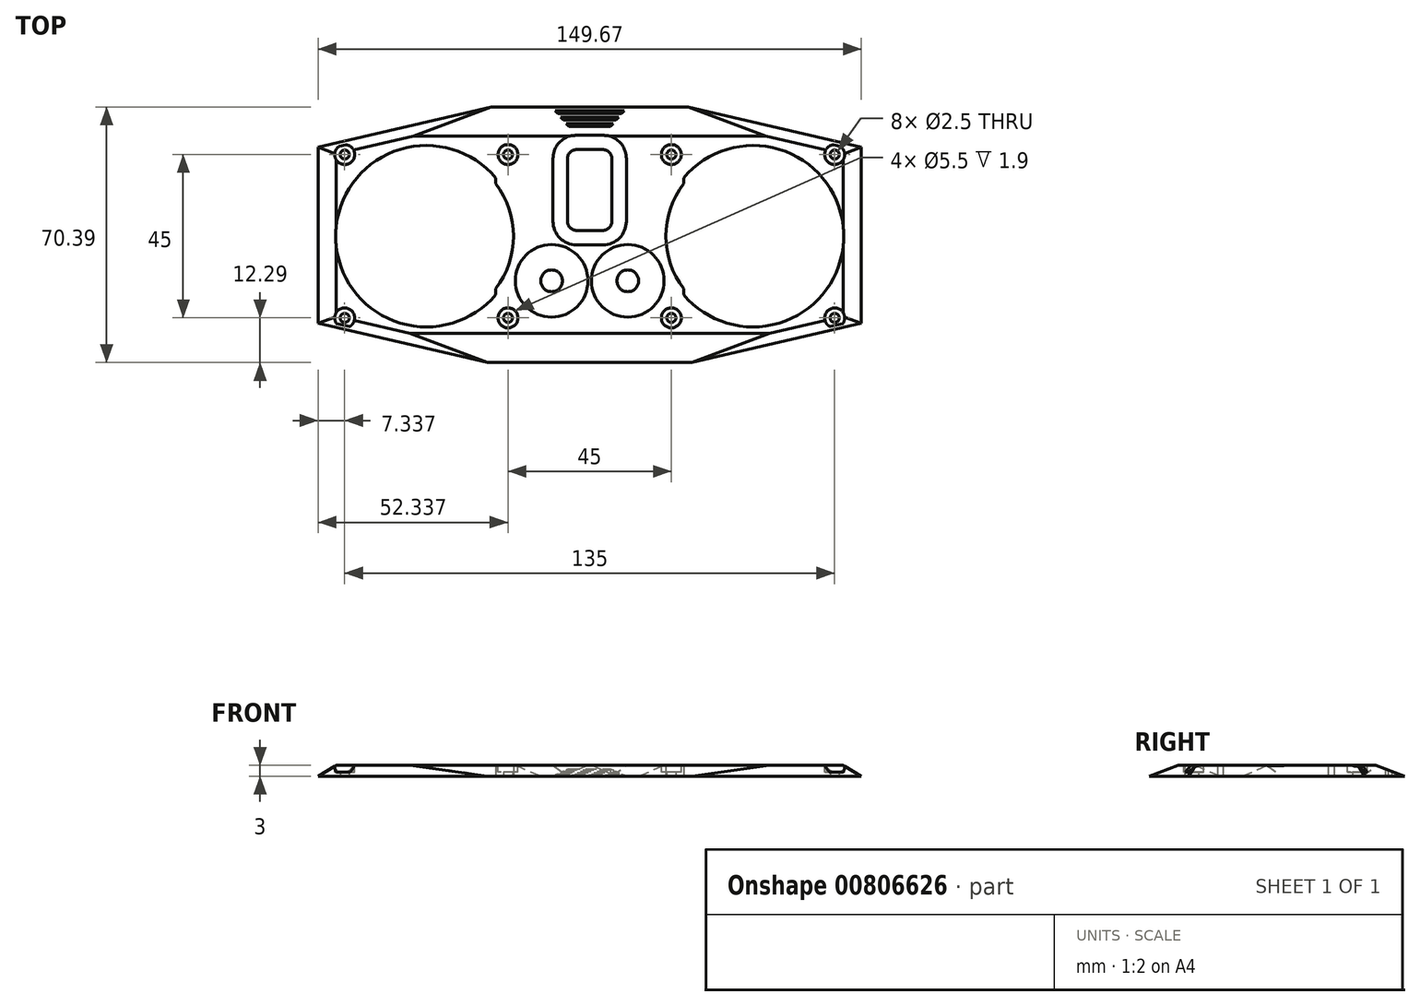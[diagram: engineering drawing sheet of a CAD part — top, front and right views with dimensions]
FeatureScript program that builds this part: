
annotation { "Feature Type Name" : "Feature", "Feature Type Description" : "" }
export const myFeature = defineFeature(function(context is Context, id is Id, definition is map)
    precondition{}
    {
        {
            var Q0;
            Q0=qCreatedBy(makeId("Top.planeOp"),FACE);
            var sketch = newSketch(context, id + "F0", { "sketchPlane" : qUnion([Q0])});
            skArc(sketch, "E0.0", {"start": v(-27.05, 29.93) * mm, "mid": v(-71.2, 13.86) * mm, "end": v(-27.05, -2.2) * mm});
            skArc(sketch, "E0.1", {"start": v(-27.05, -0.6) * mm, "mid": v(-22.2, 13.86) * mm, "end": v(-27.05, 28.32) * mm});
            skLineSegment(sketch, "E0.2", {"start": v(-27.05, -2.2) * mm, "end": v(-27.05, -0.6) * mm});
            skLineSegment(sketch, "E0.3", {"start": v(-27.05, 29.93) * mm, "end": v(-27.05, 28.32) * mm});
            skCircle(sketch, "E0.4", {"center": v(-23.7, 36.36) * mm, "radius": 1.25 * mm});
            skCircle(sketch, "E0.5", {"center": v(-68.7, 36.36) * mm, "radius": 1.25 * mm});
            skLineSegment(sketch, "E0.6", {"start": v(-77.2, 39.39) * mm, "end": v(-28.53, 50.62) * mm, "construction": true});
            skLineSegment(sketch, "E0.7", {"start": v(-77.2, 39.39) * mm, "end": v(-77.2, -45.78) * mm, "construction": true});
            skLineSegment(sketch, "E0.8", {"start": v(-28.53, 50.62) * mm, "end": v(26.12, 50.62) * mm, "construction": true});
            skLineSegment(sketch, "E0.9", {"start": v(74.8, 39.39) * mm, "end": v(26.12, 50.62) * mm, "construction": true});
            skLineSegment(sketch, "E0.10", {"start": v(-12.2, 50.26) * mm, "end": v(9.8, 50.26) * mm, "construction": true});
            skLineSegment(sketch, "E0.11", {"start": v(-11.4, 49.46) * mm, "end": v(9, 49.46) * mm, "construction": true});
            skLineSegment(sketch, "E0.12", {"start": v(8.3, 48.46) * mm, "end": v(-10.7, 48.46) * mm});
            skLineSegment(sketch, "E0.13", {"start": v(7.5, 47.66) * mm, "end": v(-9.9, 47.66) * mm});
            skLineSegment(sketch, "E0.14", {"start": v(6.8, 46.66) * mm, "end": v(-9.2, 46.66) * mm});
            skLineSegment(sketch, "E0.15", {"start": v(6, 45.86) * mm, "end": v(-8.4, 45.86) * mm});
            skLineSegment(sketch, "E0.16", {"start": v(5.3, 44.86) * mm, "end": v(-7.7, 44.86) * mm});
            skLineSegment(sketch, "E0.17", {"start": v(4.5, 44.06) * mm, "end": v(-6.9, 44.06) * mm});
            skLineSegment(sketch, "E0.18", {"start": v(-5.3, 35.25) * mm, "end": v(-5.3, 17.95) * mm, "construction": true});
            skLineSegment(sketch, "E0.19", {"start": v(2.4, 35.75) * mm, "end": v(-4.8, 35.75) * mm, "construction": true});
            skLineSegment(sketch, "E0.20", {"start": v(2.9, 35.25) * mm, "end": v(2.9, 17.95) * mm, "construction": true});
            skLineSegment(sketch, "E0.21", {"start": v(2.4, 17.45) * mm, "end": v(-4.8, 17.45) * mm, "construction": true});
            skArc(sketch, "E0.22", {"start": v(-4.8, 17.45) * mm, "mid": v(-5.16, 17.6) * mm, "end": v(-5.3, 17.95) * mm, "construction": true});
            skArc(sketch, "E0.23", {"start": v(2.9, 17.95) * mm, "mid": v(2.75, 17.6) * mm, "end": v(2.4, 17.45) * mm, "construction": true});
            skArc(sketch, "E0.24", {"start": v(2.4, 35.75) * mm, "mid": v(2.75, 35.6) * mm, "end": v(2.9, 35.25) * mm, "construction": true});
            skArc(sketch, "E0.25", {"start": v(-5.3, 35.25) * mm, "mid": v(-5.16, 35.6) * mm, "end": v(-4.8, 35.75) * mm, "construction": true});
            skCircle(sketch, "E0.26", {"center": v(21.3, 36.36) * mm, "radius": 1.25 * mm});
            skCircle(sketch, "E0.27", {"center": v(66.3, 36.36) * mm, "radius": 1.25 * mm});
            skCircle(sketch, "E0.28", {"center": v(66.3, -8.64) * mm, "radius": 1.25 * mm});
            skCircle(sketch, "E0.29", {"center": v(21.3, -8.64) * mm, "radius": 1.25 * mm});
            skArc(sketch, "E0.30", {"start": v(24.64, -2.2) * mm, "mid": v(68.8, 13.86) * mm, "end": v(24.64, 29.93) * mm});
            skArc(sketch, "E0.31", {"start": v(24.64, 28.32) * mm, "mid": v(19.8, 13.86) * mm, "end": v(24.64, -0.6) * mm});
            skLineSegment(sketch, "E0.32", {"start": v(74.8, -45.78) * mm, "end": v(74.8, 39.39) * mm, "construction": true});
            skLineSegment(sketch, "E0.33", {"start": v(24.64, -2.2) * mm, "end": v(24.64, -0.6) * mm});
            skLineSegment(sketch, "E0.34", {"start": v(24.64, 29.93) * mm, "end": v(24.64, 28.32) * mm});
            skLineSegment(sketch, "E0.35", {"start": v(13.5, 10.27) * mm, "end": v(5.1, 10.27) * mm, "construction": true});
            skLineSegment(sketch, "E0.36", {"start": v(13.5, 5.77) * mm, "end": v(13.5, 10.27) * mm, "construction": true});
            skLineSegment(sketch, "E0.37", {"start": v(18, 5.77) * mm, "end": v(13.5, 5.77) * mm, "construction": true});
            skLineSegment(sketch, "E0.38", {"start": v(18, -2.63) * mm, "end": v(18, 5.77) * mm, "construction": true});
            skLineSegment(sketch, "E0.39", {"start": v(13.5, -2.63) * mm, "end": v(18, -2.63) * mm, "construction": true});
            skLineSegment(sketch, "E0.40", {"start": v(13.5, -7.13) * mm, "end": v(13.5, -2.63) * mm, "construction": true});
            skLineSegment(sketch, "E0.41", {"start": v(13.5, -7.13) * mm, "end": v(5.1, -7.13) * mm, "construction": true});
            skLineSegment(sketch, "E0.42", {"start": v(5.1, -7.13) * mm, "end": v(5.1, -2.63) * mm, "construction": true});
            skLineSegment(sketch, "E0.43", {"start": v(0.6, -2.63) * mm, "end": v(5.1, -2.63) * mm, "construction": true});
            skLineSegment(sketch, "E0.44", {"start": v(0.6, -2.63) * mm, "end": v(0.6, 5.77) * mm, "construction": true});
            skLineSegment(sketch, "E0.45", {"start": v(5.1, 5.77) * mm, "end": v(0.6, 5.77) * mm, "construction": true});
            skLineSegment(sketch, "E0.46", {"start": v(5.1, 5.77) * mm, "end": v(5.1, 10.27) * mm, "construction": true});
            skLineSegment(sketch, "E0.47", {"start": v(-3, -2.63) * mm, "end": v(-3, 5.77) * mm, "construction": true});
            skLineSegment(sketch, "E0.48", {"start": v(-7.5, 5.77) * mm, "end": v(-3, 5.77) * mm, "construction": true});
            skLineSegment(sketch, "E0.49", {"start": v(-7.5, 5.77) * mm, "end": v(-7.5, 10.27) * mm, "construction": true});
            skLineSegment(sketch, "E0.50", {"start": v(-15.9, 10.27) * mm, "end": v(-7.5, 10.27) * mm, "construction": true});
            skLineSegment(sketch, "E0.51", {"start": v(-15.9, 5.77) * mm, "end": v(-15.9, 10.27) * mm, "construction": true});
            skLineSegment(sketch, "E0.52", {"start": v(-20.4, 5.77) * mm, "end": v(-15.9, 5.77) * mm, "construction": true});
            skLineSegment(sketch, "E0.53", {"start": v(-20.4, -2.63) * mm, "end": v(-20.4, 5.77) * mm, "construction": true});
            skLineSegment(sketch, "E0.54", {"start": v(-15.9, -2.63) * mm, "end": v(-20.4, -2.63) * mm, "construction": true});
            skLineSegment(sketch, "E0.55", {"start": v(-15.9, -7.13) * mm, "end": v(-15.9, -2.63) * mm, "construction": true});
            skLineSegment(sketch, "E0.56", {"start": v(-15.9, -7.13) * mm, "end": v(-7.5, -7.13) * mm, "construction": true});
            skLineSegment(sketch, "E0.57", {"start": v(-7.5, -7.13) * mm, "end": v(-7.5, -2.63) * mm, "construction": true});
            skLineSegment(sketch, "E0.58", {"start": v(-3, -2.63) * mm, "end": v(-7.5, -2.63) * mm, "construction": true});
            skCircle(sketch, "E0.59", {"center": v(-23.7, -8.64) * mm, "radius": 1.25 * mm});
            skCircle(sketch, "E0.60", {"center": v(-53.22, -28.82) * mm, "radius": 4.05 * mm, "construction": true});
            skCircle(sketch, "E0.61", {"center": v(-53.22, -42.82) * mm, "radius": 4.05 * mm, "construction": true});
            skLineSegment(sketch, "E0.62", {"start": v(-73.07, -50.7) * mm, "end": v(-43.77, -55.87) * mm, "construction": true});
            skArc(sketch, "E0.63", {"start": v(-77.2, -45.78) * mm, "mid": v(-76.03, -48.99) * mm, "end": v(-73.07, -50.7) * mm, "construction": true});
            skLineSegment(sketch, "E0.64", {"start": v(-43.77, -55.87) * mm, "end": v(41.36, -55.87) * mm, "construction": true});
            skLineSegment(sketch, "E0.65", {"start": v(41.36, -55.87) * mm, "end": v(70.67, -50.7) * mm, "construction": true});
            skCircle(sketch, "E0.66", {"center": v(53.62, -34.26) * mm, "radius": 16.25 * mm, "construction": true});
            skArc(sketch, "E0.67", {"start": v(70.67, -50.7) * mm, "mid": v(73.63, -48.99) * mm, "end": v(74.8, -45.78) * mm, "construction": true});
            skLineSegment(sketch, "E0.68", {"start": v(-29.45, -20.93) * mm, "end": v(27.05, -20.93) * mm});
            skLineSegment(sketch, "E0.69", {"start": v(27.05, -54.93) * mm, "end": v(27.05, -20.93) * mm, "construction": true});
            skLineSegment(sketch, "E0.70", {"start": v(-29.45, -54.93) * mm, "end": v(-29.45, -20.93) * mm, "construction": true});
            skLineSegment(sketch, "E0.71", {"start": v(-29.45, -54.93) * mm, "end": v(27.05, -54.93) * mm, "construction": true});
            skCircle(sketch, "E0.72", {"center": v(-68.7, -8.64) * mm, "radius": 1.25 * mm});
            skLineSegment(sketch, "E1", {"start": v(-1.2, 35.75) * mm, "end": v(-1.2, 17.45) * mm, "construction": true});
            skLineSegment(sketch, "E2", {"start": v(-5.3, 26.6) * mm, "end": v(2.9, 26.6) * mm, "construction": true});
            skLineSegment(sketch, "E3", {"start": v(-11.7, 10.27) * mm, "end": v(-11.7, -7.13) * mm, "construction": true});
            skLineSegment(sketch, "E4", {"start": v(-20.4, 1.57) * mm, "end": v(-3, 1.57) * mm, "construction": true});
            skLineSegment(sketch, "E5", {"start": v(9.3, 10.27) * mm, "end": v(9.3, -7.13) * mm, "construction": true});
            skLineSegment(sketch, "E6", {"start": v(0.6, 1.57) * mm, "end": v(18, 1.57) * mm, "construction": true});
            skCircle(sketch, "E7", {"center": v(-11.7, 1.57) * mm, "radius": 3 * mm});
            skCircle(sketch, "E8", {"center": v(9.3, 1.57) * mm, "radius": 3 * mm});
            skLineSegment(sketch, "E9", {"start": v(-12.2, 50.26) * mm, "end": v(-11.4, 49.46) * mm, "construction": true});
            skLineSegment(sketch, "E10", {"start": v(-10.7, 48.46) * mm, "end": v(-9.9, 47.66) * mm});
            skLineSegment(sketch, "E11", {"start": v(-9.2, 46.66) * mm, "end": v(-8.4, 45.86) * mm});
            skLineSegment(sketch, "E12", {"start": v(-7.7, 44.86) * mm, "end": v(-6.9, 44.06) * mm});
            skLineSegment(sketch, "E13", {"start": v(9.8, 50.26) * mm, "end": v(9, 49.46) * mm, "construction": true});
            skLineSegment(sketch, "E14", {"start": v(8.3, 48.46) * mm, "end": v(7.5, 47.66) * mm});
            skLineSegment(sketch, "E15", {"start": v(6.8, 46.66) * mm, "end": v(6, 45.86) * mm});
            skLineSegment(sketch, "E16", {"start": v(5.3, 44.86) * mm, "end": v(4.5, 44.06) * mm});
            skArc(sketch, "E17.0", {"start": v(4.9, 17.95) * mm, "mid": v(4.17, 16.19) * mm, "end": v(2.4, 15.45) * mm});
            skLineSegment(sketch, "E17.1", {"start": v(4.9, 35.25) * mm, "end": v(4.9, 17.95) * mm});
            skLineSegment(sketch, "E17.2", {"start": v(2.4, 15.45) * mm, "end": v(-4.8, 15.45) * mm});
            skArc(sketch, "E17.3", {"start": v(2.4, 37.75) * mm, "mid": v(4.17, 37.02) * mm, "end": v(4.9, 35.25) * mm});
            skArc(sketch, "E17.4", {"start": v(-4.8, 15.45) * mm, "mid": v(-6.57, 16.19) * mm, "end": v(-7.3, 17.95) * mm});
            skLineSegment(sketch, "E17.5", {"start": v(-7.3, 35.25) * mm, "end": v(-7.3, 17.95) * mm});
            skArc(sketch, "E17.6", {"start": v(-7.3, 35.25) * mm, "mid": v(-6.57, 37.02) * mm, "end": v(-4.8, 37.75) * mm});
            skLineSegment(sketch, "E17.7", {"start": v(2.4, 37.75) * mm, "end": v(-4.8, 37.75) * mm});
            skLineSegment(sketch, "E18.0", {"start": v(73.63, -45.78) * mm, "end": v(73.63, 38.46) * mm});
            skLineSegment(sketch, "E18.1", {"start": v(-76.04, 38.46) * mm, "end": v(-76.04, -45.78) * mm});
            skLineSegment(sketch, "E18.2", {"start": v(-76.04, 38.46) * mm, "end": v(-28.4, 49.46) * mm});
            skLineSegment(sketch, "E18.3", {"start": v(-28.4, 49.46) * mm, "end": v(26, 49.46) * mm});
            skLineSegment(sketch, "E18.4", {"start": v(73.63, 38.46) * mm, "end": v(26, 49.46) * mm});
            skLineSegment(sketch, "E19", {"start": v(-76.04, -10.17) * mm, "end": v(-44.15, -17.53) * mm});
            skLineSegment(sketch, "E20", {"start": v(-29.45, -20.93) * mm, "end": v(-44.15, -17.53) * mm});
            skLineSegment(sketch, "E21", {"start": v(27.05, -20.93) * mm, "end": v(73.63, -10.17) * mm});
            skSolve(sketch);
        }
        {
            var Q0;
            Q0=makeQuery(id+"F0.imprint","IMPRINT",FACE,{"disambiguationData":[TD([[makeQuery(id+"F0.imprint","IMPRINT",EDGE,{"derivedFrom":sQuery(id+"F0.wireOp",EDGE,"E0.0")}),-1.0]])]});
            extrude(context, id + "F1", {"entities" : qUnion([Q0]), "depth" : 3 * mm, "offsetDistance" : 25 * mm});
        }
        {
            var Q0;
            Q0=makeQuery(id+"F1.opExtrude","CAP_EDGE",EDGE,{"disambiguationData":[OSD([sQuery(id+"F0.wireOp",EDGE,"E8")])],"isStart":false});
            var Q1;
            Q1=makeQuery(id+"F1.opExtrude","CAP_EDGE",EDGE,{"disambiguationData":[OSD([sQuery(id+"F0.wireOp",EDGE,"E7")])],"isStart":false});
            chamfer(context, id + "F2", {"entities" : qUnion([Q0, Q1]), "chamferType" : ChamferType.TWO_OFFSETS, "width1" : 3 * mm, "oppositeDirection" : false, "width2" : 7 * mm, "tangentPropagation" : true});
        }
        {
            var Q0;
            Q0=makeQuery(id+"F1.opExtrude","CAP_EDGE",EDGE,{"disambiguationData":[OSD([sQuery(id+"F0.wireOp",EDGE,"E17.7")])],"isStart":false});
            var Q1;
            Q1=makeQuery(id+"F1.opExtrude","CAP_EDGE",EDGE,{"disambiguationData":[OSD([sQuery(id+"F0.wireOp",EDGE,"E17.5")])],"isStart":false});
            var Q2;
            Q2=makeQuery(id+"F1.opExtrude","CAP_EDGE",EDGE,{"disambiguationData":[OSD([sQuery(id+"F0.wireOp",EDGE,"E17.2")])],"isStart":false});
            var Q3;
            Q3=makeQuery(id+"F1.opExtrude","CAP_EDGE",EDGE,{"disambiguationData":[OSD([sQuery(id+"F0.wireOp",EDGE,"E17.4")])],"isStart":false});
            var Q4;
            Q4=makeQuery(id+"F1.opExtrude","CAP_EDGE",EDGE,{"disambiguationData":[OSD([sQuery(id+"F0.wireOp",EDGE,"E17.0")])],"isStart":false});
            var Q5;
            Q5=makeQuery(id+"F1.opExtrude","CAP_EDGE",EDGE,{"disambiguationData":[OSD([sQuery(id+"F0.wireOp",EDGE,"E17.1")])],"isStart":false});
            var Q6;
            Q6=makeQuery(id+"F1.opExtrude","CAP_EDGE",EDGE,{"disambiguationData":[OSD([sQuery(id+"F0.wireOp",EDGE,"E17.3")])],"isStart":false});
            var Q7;
            Q7=makeQuery(id+"F1.opExtrude","CAP_EDGE",EDGE,{"disambiguationData":[OSD([sQuery(id+"F0.wireOp",EDGE,"E17.6")])],"isStart":false});
            chamfer(context, id + "F3", {"entities" : qUnion([Q0, Q1, Q2, Q3, Q4, Q5, Q6, Q7]), "chamferType" : ChamferType.TWO_OFFSETS, "width1" : 3 * mm, "oppositeDirection" : false, "width2" : 4 * mm, "tangentPropagation" : true});
        }
        {
            var Q0;
            Q0=makeQuery(id+"F1.opExtrude","CAP_EDGE",EDGE,{"disambiguationData":[OSD([sQuery(id+"F0.wireOp",EDGE,"E18.3")])],"isStart":false});
            var Q1;
            Q1=makeQuery(id+"F1.opExtrude","CAP_EDGE",EDGE,{"disambiguationData":[OSD([sQuery(id+"F0.wireOp",EDGE,"E0.68")])],"isStart":false});
            chamfer(context, id + "F4", {"entities" : qUnion([Q0, Q1]), "chamferType" : ChamferType.TWO_OFFSETS, "width1" : 3 * mm, "oppositeDirection" : false, "width2" : 8 * mm, "tangentPropagation" : true});
        }
        {
            var Q0;
            Q0=makeQuery(id+"F1.opExtrude","CAP_EDGE",EDGE,{"disambiguationData":[OSD([sQuery(id+"F0.wireOp",EDGE,"E18.1")])],"isStart":false});
            var Q1;
            Q1=makeQuery(id+"F1.opExtrude","CAP_EDGE",EDGE,{"disambiguationData":[OSD([sQuery(id+"F0.wireOp",EDGE,"E18.0")])],"isStart":false});
            chamfer(context, id + "F5", {"entities" : qUnion([Q0, Q1]), "chamferType" : ChamferType.TWO_OFFSETS, "width1" : 5 * mm, "oppositeDirection" : false, "width2" : 3 * mm, "tangentPropagation" : true});
        }
        {
            var Q0;
            Q0=makeQuery(id+"F1.opExtrude","CAP_EDGE",EDGE,{"disambiguationData":[OSD([sQuery(id+"F0.wireOp",EDGE,"E19"),sQuery(id+"F0.wireOp",EDGE,"E20")])],"isStart":false});
            var Q1;
            Q1=makeQuery(id+"F1.opExtrude","CAP_EDGE",EDGE,{"disambiguationData":[OSD([sQuery(id+"F0.wireOp",EDGE,"E18.2")])],"isStart":false});
            var Q2;
            Q2=makeQuery(id+"F1.opExtrude","CAP_EDGE",EDGE,{"disambiguationData":[OSD([sQuery(id+"F0.wireOp",EDGE,"E21")])],"isStart":false});
            var Q3;
            Q3=makeQuery(id+"F1.opExtrude","CAP_EDGE",EDGE,{"disambiguationData":[OSD([sQuery(id+"F0.wireOp",EDGE,"E18.4")])],"isStart":false});
            chamfer(context, id + "F6", {"entities" : qUnion([Q0, Q1, Q2, Q3]), "chamferType" : ChamferType.TWO_OFFSETS, "width1" : 3 * mm, "oppositeDirection" : false, "width2" : 3 * mm, "tangentPropagation" : true});
        }
        {
            var Q0;
            Q0=makeQuery(id+"F1.opExtrude","CAP_FACE",FACE,{"disambiguationData":[OSD([sQuery(id+"F0.wireOp",EDGE,"E0.0"),sQuery(id+"F0.wireOp",EDGE,"E0.1"),sQuery(id+"F0.wireOp",EDGE,"E0.2"),sQuery(id+"F0.wireOp",EDGE,"E0.3"),sQuery(id+"F0.wireOp",EDGE,"E0.4"),sQuery(id+"F0.wireOp",EDGE,"E0.5"),sQuery(id+"F0.wireOp",EDGE,"E0.12"),sQuery(id+"F0.wireOp",EDGE,"E0.13"),sQuery(id+"F0.wireOp",EDGE,"E0.14"),sQuery(id+"F0.wireOp",EDGE,"E0.15"),sQuery(id+"F0.wireOp",EDGE,"E0.16"),sQuery(id+"F0.wireOp",EDGE,"E0.17"),sQuery(id+"F0.wireOp",EDGE,"E0.26"),sQuery(id+"F0.wireOp",EDGE,"E0.27"),sQuery(id+"F0.wireOp",EDGE,"E0.28"),sQuery(id+"F0.wireOp",EDGE,"E0.29"),sQuery(id+"F0.wireOp",EDGE,"E0.30"),sQuery(id+"F0.wireOp",EDGE,"E0.31"),sQuery(id+"F0.wireOp",EDGE,"E0.33"),sQuery(id+"F0.wireOp",EDGE,"E0.34"),sQuery(id+"F0.wireOp",EDGE,"E0.59"),sQuery(id+"F0.wireOp",EDGE,"E0.68"),sQuery(id+"F0.wireOp",EDGE,"E0.72"),sQuery(id+"F0.wireOp",EDGE,"E7"),sQuery(id+"F0.wireOp",EDGE,"E8"),sQuery(id+"F0.wireOp",EDGE,"E10"),sQuery(id+"F0.wireOp",EDGE,"E11"),sQuery(id+"F0.wireOp",EDGE,"E12"),sQuery(id+"F0.wireOp",EDGE,"E14"),sQuery(id+"F0.wireOp",EDGE,"E15"),sQuery(id+"F0.wireOp",EDGE,"E16"),sQuery(id+"F0.wireOp",EDGE,"E17.0"),sQuery(id+"F0.wireOp",EDGE,"E17.1"),sQuery(id+"F0.wireOp",EDGE,"E17.2"),sQuery(id+"F0.wireOp",EDGE,"E17.3"),sQuery(id+"F0.wireOp",EDGE,"E17.4"),sQuery(id+"F0.wireOp",EDGE,"E17.5"),sQuery(id+"F0.wireOp",EDGE,"E17.6"),sQuery(id+"F0.wireOp",EDGE,"E17.7"),sQuery(id+"F0.wireOp",EDGE,"E18.0"),sQuery(id+"F0.wireOp",EDGE,"E18.1"),sQuery(id+"F0.wireOp",EDGE,"E18.2"),sQuery(id+"F0.wireOp",EDGE,"E18.3"),sQuery(id+"F0.wireOp",EDGE,"E18.4"),sQuery(id+"F0.wireOp",EDGE,"E19"),sQuery(id+"F0.wireOp",EDGE,"E20"),sQuery(id+"F0.wireOp",EDGE,"E21")])],"isStart":false});
            var sketch = newSketch(context, id + "F7", { "sketchPlane" : qUnion([Q0])});
            skCircle(sketch, "E22.0", {"center": v(-23.7, 36.36) * mm, "radius": 1.25 * mm});
            skCircle(sketch, "E22.1", {"center": v(21.3, 36.36) * mm, "radius": 1.25 * mm});
            skCircle(sketch, "E22.2", {"center": v(66.3, 36.36) * mm, "radius": 1.25 * mm});
            skCircle(sketch, "E22.3", {"center": v(66.3, -8.64) * mm, "radius": 1.25 * mm});
            skCircle(sketch, "E22.4", {"center": v(21.3, -8.64) * mm, "radius": 1.25 * mm});
            skCircle(sketch, "E22.5", {"center": v(-23.7, -8.64) * mm, "radius": 1.25 * mm});
            skCircle(sketch, "E22.6", {"center": v(-68.7, -8.64) * mm, "radius": 1.25 * mm});
            skCircle(sketch, "E22.7", {"center": v(-68.7, 36.36) * mm, "radius": 1.25 * mm});
            skCircle(sketch, "E23", {"center": v(-68.7, 36.36) * mm, "radius": 2.75 * mm});
            skCircle(sketch, "E24", {"center": v(-23.7, 36.36) * mm, "radius": 2.75 * mm});
            skCircle(sketch, "E25", {"center": v(21.3, 36.36) * mm, "radius": 2.75 * mm});
            skCircle(sketch, "E26", {"center": v(66.3, 36.36) * mm, "radius": 2.75 * mm});
            skCircle(sketch, "E27", {"center": v(66.3, -8.64) * mm, "radius": 2.75 * mm});
            skCircle(sketch, "E28", {"center": v(21.3, -8.64) * mm, "radius": 2.75 * mm});
            skCircle(sketch, "E29", {"center": v(-23.7, -8.64) * mm, "radius": 2.75 * mm});
            skCircle(sketch, "E30", {"center": v(-68.7, -8.64) * mm, "radius": 2.75 * mm});
            skSolve(sketch);
        }
        {
            var Q0;
            Q0=qSketchRegion(id+"F7",true);
            extrude(context, id + "F8", {"entities" : qUnion([Q0]), "operationType" : NewBodyOperationType.REMOVE, "oppositeDirection" : true, "depth" : 1.9 * mm, "offsetDistance" : 25 * mm});
        }
    });
